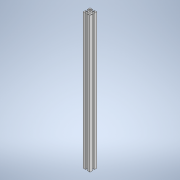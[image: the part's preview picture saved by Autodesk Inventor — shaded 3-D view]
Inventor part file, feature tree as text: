
AUTODESK INVENTOR PART (.ipt)
format: ipt  version: 2022 (Build 260153000, 153)  size: 154,624 bytes
history: native  units: in
note: dims shown in document units (in); Inventor stores cm internally (conversion verified against a paired STEP export)
features: sketch x2, extrude x1, hole x1
ambient origin geometry x8: Origin, YZ Plane, XZ Plane, XY Plane, X Axis, Y Axis, Z Axis, Center Point
bodies: Body1 (feature_tree)
feature tree (4):
  extrude  "Extrusion1"  [1 undecoded]
  hole  "Hole1"  [1 undecoded]
  sketch  "Sketch1"  dims[d0=15.748in d1=0.0in]
  sketch  "Sketch2"  dims[d2=0.1575in d3=0.2362in d4=0.1575in d5=0.0787in d6=90.0deg d7=0.315in d8=0.8108in]
note: 2 required parameter values undecoded (feature->parameter linkage not recoverable at this tier; creation-order binding heuristic only, values carry confidence <= 0.55)
